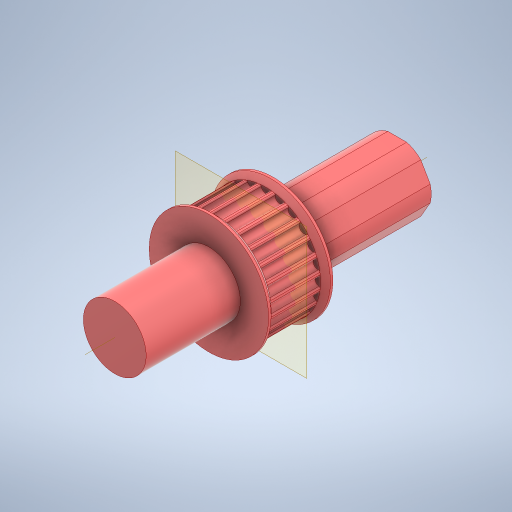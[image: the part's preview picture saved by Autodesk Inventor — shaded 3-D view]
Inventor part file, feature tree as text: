
AUTODESK INVENTOR PART (.ipt)
format: ipt  version: 2023.3 (Build 273359000, 359)  size: 550,400 bytes
history: native  units: in
note: dims shown in document units (in); Inventor stores cm internally (conversion verified against a paired STEP export)
features: extrude x9, sketch x9, mirror x2, chamfer x2, projected_geometry x2, other x1, fillet x1, pattern_circular x1
ambient origin geometry x8: Origin, YZ Plane, XZ Plane, XY Plane, X Axis, Y Axis, Z Axis, Center Point
bodies: Solid1 (feature_tree)
feature tree (27):
  other  "Hex Bore"
  extrude  "HTD Base"  Depth=0.3937in TaperAngle=0.0deg
  extrude  "HTD Flange"  Depth=0.0591in
  mirror  "HTD Flanges"
  chamfer  "HTD Flange Chamfer"  Distance=0.0787in Angle=45.0deg
  extrude  "GT2 Base"  TaperAngle=0.0deg  [1 undecoded]
  extrude  "GT2 Base Tooth"  TaperAngle=0.0deg  [1 undecoded]
  fillet  "GT2 Base Tooth pt. 2"  Radius=0.8723in
  pattern_circular  "GT2 Teeth"  [2 undecoded]
  extrude  "GT2 Flange"  TaperAngle=0.0deg  [1 undecoded]
  mirror  "GT2 Flanges"
  chamfer  "GT2 Flange Chamfer"  Distance=0.0118in
  extrude  "Circle Bore"  Depth=0.3937in
  extrude  "Extrusion9"  TaperAngle=360.0deg  [1 undecoded]
  extrude  "Extrusion10"  Depth=0.3937in
  extrude  "Extrusion11"  Depth=0.0591in
  sketch  "Sketch1"  dims[d0=1.4588in d1=0.3937in d2=0.0in]
  sketch  "Sketch4"  dims[d12=0.0394in d13=0.0591in]
  sketch  "Sketch5"  dims[d14=0.0in]
  sketch  "Sketch6"  dims[d15=0.0394in d16=0.0787in d17=45.0deg]
  sketch  "Sketch7"  dims[d18=0.52in d19=0.0in d20=0.0in]
  sketch  "Sketch8"  dims[d21=0.52in d22=0.0in d23=0.0in d24=0.8723in]
  sketch  "Sketch9"  dims[d25=0.3937in]
  projected_geometry  "Projected Loop1"
  sketch  "Sketch10"  dims[d26=0.0in]
  sketch  "Sketch11"  dims[d27=0.0727in d28=0.0075in d29=0.0in d30=0.0in d31=0.0118in d32=9.4488in d33=360.0deg d35=0.0394in d36=0.0591in d37=0.0in d38=0.0394in d39=0.0787in d40=45.0deg d41=1.5in d42=0.0in d43=0.5in d44=0.75in d45=0.0in d46=0.5413in d47=0.3937in d48=0.0in d49=0.0197in d50=0.0344in]
  projected_geometry  "Projected Loop2"
note: 6 required parameter values undecoded (feature->parameter linkage not recoverable at this tier; creation-order binding heuristic only, values carry confidence <= 0.55)
